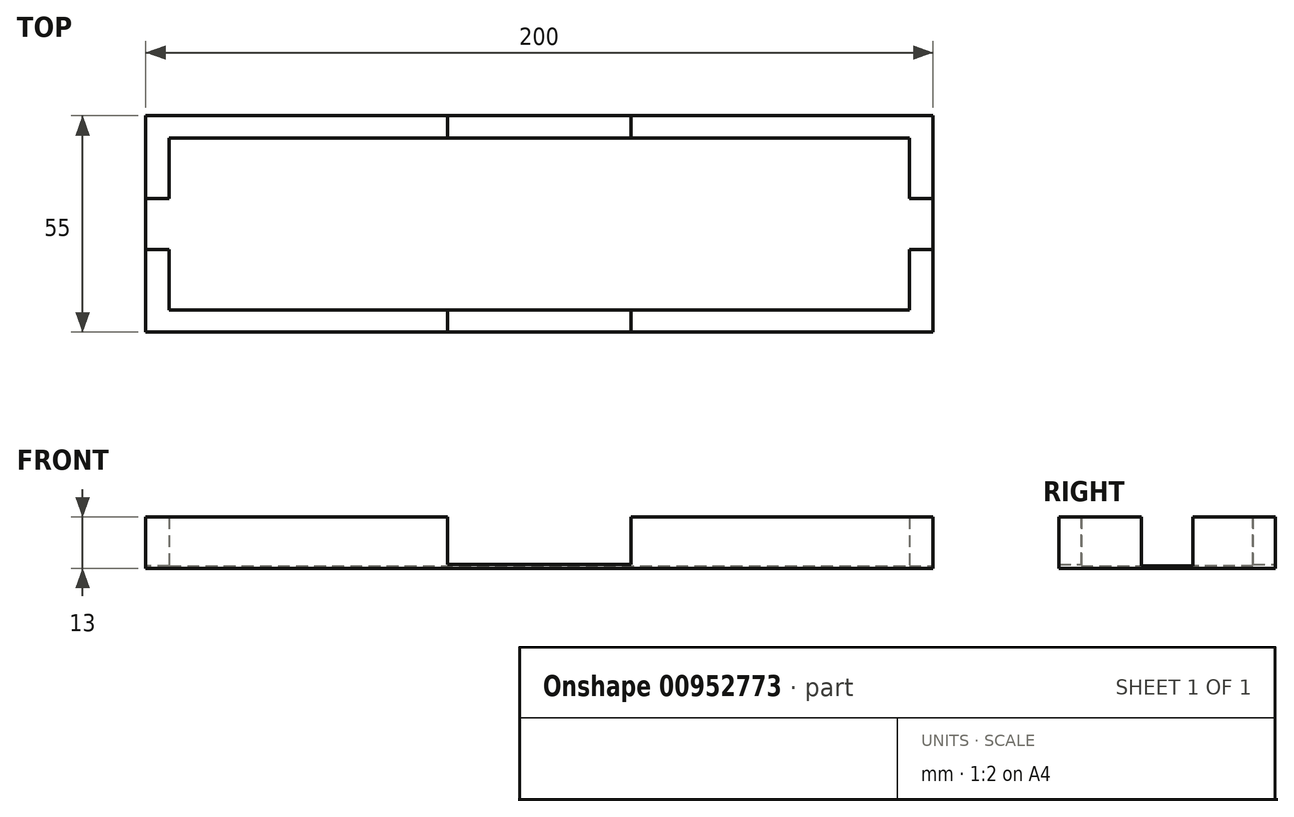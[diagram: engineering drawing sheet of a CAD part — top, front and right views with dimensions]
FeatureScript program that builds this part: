
annotation { "Feature Type Name" : "Feature", "Feature Type Description" : "" }
export const myFeature = defineFeature(function(context is Context, id is Id, definition is map)
    precondition{}
    {
        {
            var Q0;
            Q0=qCreatedBy(makeId("Top.planeOp"),FACE);
            var sketch = newSketch(context, id + "F0", { "sketchPlane" : qUnion([Q0])});
            skLineSegment(sketch, "E0.bottom", {"start": v(100, -27.5) * mm, "end": v(-100, -27.5) * mm});
            skLineSegment(sketch, "E0.top", {"start": v(100, 27.5) * mm, "end": v(-100, 27.5) * mm});
            skLineSegment(sketch, "E0.left", {"start": v(100, -27.5) * mm, "end": v(100, 27.5) * mm});
            skLineSegment(sketch, "E0.right", {"start": v(-100, -27.5) * mm, "end": v(-100, 27.5) * mm});
            skPoint(sketch, "E0.middle", {"position": v(0, 0) * mm});
            skLineSegment(sketch, "E1.bottom", {"start": v(100, -6.5) * mm, "end": v(94, -6.5) * mm});
            skLineSegment(sketch, "E1.top", {"start": v(100, 6.5) * mm, "end": v(94, 6.5) * mm});
            skLineSegment(sketch, "E1.right", {"start": v(94, -6.5) * mm, "end": v(94, 6.5) * mm});
            skPoint(sketch, "E1.middle", {"position": v(100, 0) * mm});
            skLineSegment(sketch, "E2.MirrorCS", {"start": v(-100, 6.5) * mm, "end": v(-94, 6.5) * mm});
            skLineSegment(sketch, "E3.MirrorCS", {"start": v(-100, -6.5) * mm, "end": v(-94, -6.5) * mm});
            skLineSegment(sketch, "E4.MirrorCS", {"start": v(-94, -6.5) * mm, "end": v(-94, 6.5) * mm});
            skPoint(sketch, "E5.orphan", {"position": v(-106, 6.5) * mm});
            skPoint(sketch, "E6.MirrorCS.start.orphan", {"position": v(-106, -6.5) * mm});
            skPoint(sketch, "E1.left.end.orphan", {"position": v(106, 6.5) * mm});
            skPoint(sketch, "E7.orphan", {"position": v(106, -6.5) * mm});
            skLineSegment(sketch, "E8", {"start": v(-100, 6.5) * mm, "end": v(-100, -6.5) * mm});
            skLineSegment(sketch, "E9", {"start": v(100, 6.5) * mm, "end": v(100, -6.5) * mm});
            skLineSegment(sketch, "E10", {"start": v(94, 6.5) * mm, "end": v(94, 27.5) * mm});
            skLineSegment(sketch, "E11", {"start": v(94, 27.5) * mm, "end": v(94, -6.5) * mm});
            skLineSegment(sketch, "E12", {"start": v(94, -27.5) * mm, "end": v(94, -6.5) * mm});
            skLineSegment(sketch, "E13", {"start": v(94, -21.83) * mm, "end": v(-100, -21.83) * mm});
            skLineSegment(sketch, "E14", {"start": v(-94, -6.5) * mm, "end": v(-94, -27.5) * mm});
            skLineSegment(sketch, "E15", {"start": v(-94, 6.5) * mm, "end": v(-94, 27.5) * mm});
            skLineSegment(sketch, "E16.MirrorCS", {"start": v(94, 21.83) * mm, "end": v(-100, 21.83) * mm});
            skSolve(sketch);
        }
        {
            var Q0;
            {var subQ8=sQuery(id+"F0.wireOp",EDGE,"E4.MirrorCS");Q0=makeQuery(id+"F0.imprint","IMPRINT",FACE,{"disambiguationData":[TD([[makeQuery(id+"F0.imprint","IMPRINT",EDGE,{"derivedFrom":subQ8}),-1.0]])]});}
            var Q1;
            {var subQ6=sQuery(id+"F0.wireOp",EDGE,"E1.top");Q1=makeQuery(id+"F0.imprint","IMPRINT",FACE,{"disambiguationData":[TD([[makeQuery(id+"F0.imprint","IMPRINT",EDGE,{"derivedFrom":subQ6}),-1.0]])]});}
            var Q2;
            {var subQ0=sQuery(id+"F0.wireOp",EDGE,"E1.bottom");Q2=makeQuery(id+"F0.imprint","IMPRINT",FACE,{"disambiguationData":[TD([[makeQuery(id+"F0.imprint","IMPRINT",EDGE,{"derivedFrom":subQ0}),-1.0]])]});}
            var Q3;
            {var subQ6=sQuery(id+"F0.wireOp",EDGE,"E1.bottom");Q3=makeQuery(id+"F0.imprint","IMPRINT",FACE,{"disambiguationData":[TD([[makeQuery(id+"F0.imprint","IMPRINT",EDGE,{"derivedFrom":subQ6}),1.0]])]});}
            var Q4;
            {var subQ0=sQuery(id+"F0.wireOp",EDGE,"E12");var subQ1=sQuery(id+"F0.wireOp",EDGE,"E0.bottom");var subQ2=makeQuery(id+"F0.imprint","INTERSECT",VERTEX,{"derivedFrom":[subQ1,subQ0]});Q4=makeQuery(id+"F0.imprint","IMPRINT",FACE,{"disambiguationData":[TD([[makeQuery(id+"F0.imprint","IMPRINT",EDGE,{"disambiguationData":[TD([[subQ2,-1.0]])],"derivedFrom":subQ1}),-1.0]])]});}
            var Q5;
            {var subQ0=sQuery(id+"F0.wireOp",EDGE,"E0.right");var subQ1=sQuery(id+"F0.wireOp",EDGE,"E0.bottom");var subQ2=makeQuery(id+"F0.imprint","INTERSECT",VERTEX,{"derivedFrom":[subQ1,subQ0]});Q5=makeQuery(id+"F0.imprint","IMPRINT",FACE,{"disambiguationData":[TD([[makeQuery(id+"F0.imprint","IMPRINT",EDGE,{"disambiguationData":[TD([[subQ2,1.0]])],"derivedFrom":subQ1}),-1.0]])]});}
            var Q6;
            {var subQ0=sQuery(id+"F0.wireOp",EDGE,"E3.MirrorCS");Q6=makeQuery(id+"F0.imprint","IMPRINT",FACE,{"disambiguationData":[TD([[makeQuery(id+"F0.imprint","IMPRINT",EDGE,{"derivedFrom":subQ0}),-1.0]])]});}
            var Q7;
            {var subQ0=sQuery(id+"F0.wireOp",EDGE,"E11");var subQ1=sQuery(id+"F0.wireOp",EDGE,"E0.top");var subQ2=makeQuery(id+"F0.imprint","INTERSECT",VERTEX,{"derivedFrom":[subQ1,subQ0]});Q7=makeQuery(id+"F0.imprint","IMPRINT",FACE,{"disambiguationData":[TD([[makeQuery(id+"F0.imprint","IMPRINT",EDGE,{"disambiguationData":[TD([[subQ2,-1.0]])],"derivedFrom":subQ1}),1.0]])]});}
            var Q8;
            {var subQ0=sQuery(id+"F0.wireOp",EDGE,"E0.right");var subQ1=sQuery(id+"F0.wireOp",EDGE,"E0.top");var subQ2=makeQuery(id+"F0.imprint","INTERSECT",VERTEX,{"derivedFrom":[subQ1,subQ0]});Q8=makeQuery(id+"F0.imprint","IMPRINT",FACE,{"disambiguationData":[TD([[makeQuery(id+"F0.imprint","IMPRINT",EDGE,{"disambiguationData":[TD([[subQ2,1.0]])],"derivedFrom":subQ1}),1.0]])]});}
            var Q9;
            {var subQ0=sQuery(id+"F0.wireOp",EDGE,"E2.MirrorCS");Q9=makeQuery(id+"F0.imprint","IMPRINT",FACE,{"disambiguationData":[TD([[makeQuery(id+"F0.imprint","IMPRINT",EDGE,{"derivedFrom":subQ0}),1.0]])]});}
            var Q10;
            Q10=makeQuery(id+"F0.imprint","IMPRINT",FACE,{"disambiguationData":[TD([[makeQuery(id+"F0.imprint","IMPRINT",EDGE,{"derivedFrom":sQuery(id+"F0.wireOp",EDGE,"E2.MirrorCS")}),-1.0]])]});
            extrude(context, id + "F1", {"entities" : qUnion([Q0, Q1, Q2, Q3, Q4, Q5, Q6, Q7, Q8, Q9, Q10]), "depth" : 0.6 * mm, "offsetDistance" : 25.4 * mm});
        }
        {
            var Q0;
            {var subQ0=sQuery(id+"F0.wireOp",EDGE,"E11");var subQ1=sQuery(id+"F0.wireOp",EDGE,"E0.top");var subQ2=makeQuery(id+"F0.imprint","INTERSECT",VERTEX,{"derivedFrom":[subQ1,subQ0]});Q0=makeQuery(id+"F0.imprint","IMPRINT",FACE,{"disambiguationData":[TD([[makeQuery(id+"F0.imprint","IMPRINT",EDGE,{"disambiguationData":[TD([[subQ2,-1.0]])],"derivedFrom":subQ1}),1.0]])]});}
            var Q1;
            {var subQ0=sQuery(id+"F0.wireOp",EDGE,"E0.right");var subQ1=sQuery(id+"F0.wireOp",EDGE,"E0.top");var subQ2=makeQuery(id+"F0.imprint","INTERSECT",VERTEX,{"derivedFrom":[subQ1,subQ0]});Q1=makeQuery(id+"F0.imprint","IMPRINT",FACE,{"disambiguationData":[TD([[makeQuery(id+"F0.imprint","IMPRINT",EDGE,{"disambiguationData":[TD([[subQ2,1.0]])],"derivedFrom":subQ1}),1.0]])]});}
            var Q2;
            {var subQ0=sQuery(id+"F0.wireOp",EDGE,"E2.MirrorCS");Q2=makeQuery(id+"F0.imprint","IMPRINT",FACE,{"disambiguationData":[TD([[makeQuery(id+"F0.imprint","IMPRINT",EDGE,{"derivedFrom":subQ0}),1.0]])]});}
            var Q3;
            {var subQ0=sQuery(id+"F0.wireOp",EDGE,"E3.MirrorCS");Q3=makeQuery(id+"F0.imprint","IMPRINT",FACE,{"disambiguationData":[TD([[makeQuery(id+"F0.imprint","IMPRINT",EDGE,{"derivedFrom":subQ0}),-1.0]])]});}
            var Q4;
            {var subQ0=sQuery(id+"F0.wireOp",EDGE,"E0.right");var subQ1=sQuery(id+"F0.wireOp",EDGE,"E0.bottom");var subQ2=makeQuery(id+"F0.imprint","INTERSECT",VERTEX,{"derivedFrom":[subQ1,subQ0]});Q4=makeQuery(id+"F0.imprint","IMPRINT",FACE,{"disambiguationData":[TD([[makeQuery(id+"F0.imprint","IMPRINT",EDGE,{"disambiguationData":[TD([[subQ2,1.0]])],"derivedFrom":subQ1}),-1.0]])]});}
            var Q5;
            {var subQ0=sQuery(id+"F0.wireOp",EDGE,"E12");var subQ1=sQuery(id+"F0.wireOp",EDGE,"E0.bottom");var subQ2=makeQuery(id+"F0.imprint","INTERSECT",VERTEX,{"derivedFrom":[subQ1,subQ0]});Q5=makeQuery(id+"F0.imprint","IMPRINT",FACE,{"disambiguationData":[TD([[makeQuery(id+"F0.imprint","IMPRINT",EDGE,{"disambiguationData":[TD([[subQ2,-1.0]])],"derivedFrom":subQ1}),-1.0]])]});}
            var Q6;
            {var subQ6=sQuery(id+"F0.wireOp",EDGE,"E1.bottom");Q6=makeQuery(id+"F0.imprint","IMPRINT",FACE,{"disambiguationData":[TD([[makeQuery(id+"F0.imprint","IMPRINT",EDGE,{"derivedFrom":subQ6}),1.0]])]});}
            var Q7;
            {var subQ6=sQuery(id+"F0.wireOp",EDGE,"E1.top");Q7=makeQuery(id+"F0.imprint","IMPRINT",FACE,{"disambiguationData":[TD([[makeQuery(id+"F0.imprint","IMPRINT",EDGE,{"derivedFrom":subQ6}),-1.0]])]});}
            extrude(context, id + "F2", {"entities" : qUnion([Q0, Q1, Q2, Q3, Q4, Q5, Q6, Q7]), "operationType" : NewBodyOperationType.ADD, "depth" : 13 * mm, "offsetDistance" : 25.4 * mm});
        }
        {
            var Q0;
            Q0=makeQuery(id+"F2.opExtrude","CAP_FACE",FACE,{"disambiguationData":[OSD([sQuery(id+"F0.wireOp",EDGE,"E0.top"),sQuery(id+"F0.wireOp",EDGE,"E0.left"),sQuery(id+"F0.wireOp",EDGE,"E0.right"),sQuery(id+"F0.wireOp",EDGE,"E1.top"),sQuery(id+"F0.wireOp",EDGE,"E2.MirrorCS"),sQuery(id+"F0.wireOp",EDGE,"E11"),sQuery(id+"F0.wireOp",EDGE,"E15"),sQuery(id+"F0.wireOp",EDGE,"E16.MirrorCS")])],"isStart":false});
            var sketch = newSketch(context, id + "F3", { "sketchPlane" : qUnion([Q0])});
            skLineSegment(sketch, "E17.bottom", {"start": v(23.31, -36.7) * mm, "end": v(-23.31, -36.7) * mm});
            skLineSegment(sketch, "E17.top", {"start": v(23.31, 36.7) * mm, "end": v(-23.31, 36.7) * mm});
            skLineSegment(sketch, "E17.left", {"start": v(23.31, -36.7) * mm, "end": v(23.31, 36.7) * mm});
            skLineSegment(sketch, "E17.right", {"start": v(-23.31, -36.7) * mm, "end": v(-23.31, 36.7) * mm});
            skPoint(sketch, "E17.middle", {"position": v(0, 0) * mm});
            skSolve(sketch);
        }
        {
            var Q0;
            {var subQ0=sQuery(id+"F3.wireOp",EDGE,"E17.bottom");Q0=makeQuery(id+"F3.imprint","IMPRINT",FACE,{"disambiguationData":[TD([[makeQuery(id+"F3.imprint","IMPRINT",EDGE,{"derivedFrom":subQ0}),-1.0]])]});}
            var Q1;
            {var subQ0=sQuery(id+"F3.wireOp",EDGE,"E17.top");Q1=makeQuery(id+"F3.imprint","IMPRINT",FACE,{"disambiguationData":[TD([[makeQuery(id+"F3.imprint","IMPRINT",EDGE,{"derivedFrom":subQ0}),1.0]])]});}
            var Q2;
            {var subQ0=sQuery(id+"F3.wireOp",EDGE,"E17.left");var subQ1=makeQuery(id+"F2.opExtrude","CAP_EDGE",EDGE,{"disambiguationData":[OSD([sQuery(id+"F0.wireOp",EDGE,"E16.MirrorCS")])],"isStart":false});var subQ2=makeQuery(id+"F3.imprint","INTERSECT",VERTEX,{"derivedFrom":[subQ1,subQ0]});Q2=makeQuery(id+"F3.imprint","IMPRINT",FACE,{"disambiguationData":[TD([[makeQuery(id+"F3.imprint","IMPRINT",EDGE,{"disambiguationData":[TD([[subQ2,-1.0]])],"derivedFrom":subQ0}),1.0]])]});}
            extrude(context, id + "F4", {"entities" : qUnion([Q0, Q1, Q2]), "operationType" : NewBodyOperationType.REMOVE, "oppositeDirection" : true, "depth" : 12 * mm, "offsetDistance" : 25.4 * mm});
        }
    });
